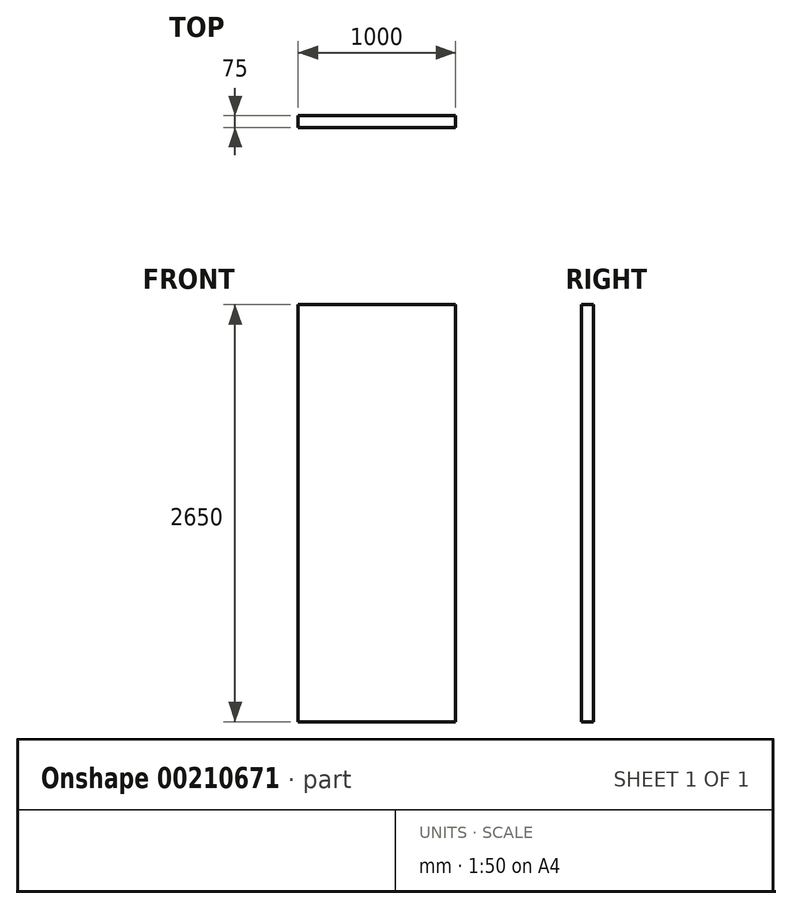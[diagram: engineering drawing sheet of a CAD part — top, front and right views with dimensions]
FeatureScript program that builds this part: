
annotation { "Feature Type Name" : "Feature", "Feature Type Description" : "" }
export const myFeature = defineFeature(function(context is Context, id is Id, definition is map)
    precondition{}
    {
        {
            var Q0;
            Q0=qCreatedBy(makeId("Front.planeOp"),FACE);
            var sketch = newSketch(context, id + "F0", { "sketchPlane" : qUnion([Q0])});
            skLineSegment(sketch, "E0.bottom", {"start": v(0, 0) * mm, "end": v(1000, 0) * mm});
            skLineSegment(sketch, "E0.top", {"start": v(0, 2650) * mm, "end": v(1000, 2650) * mm});
            skLineSegment(sketch, "E0.left", {"start": v(0, 0) * mm, "end": v(0, 2650) * mm});
            skLineSegment(sketch, "E0.right", {"start": v(1000, 0) * mm, "end": v(1000, 2650) * mm});
            skSolve(sketch);
        }
        {
            var Q0;
            Q0=makeQuery(id+"F0.imprint","IMPRINT",FACE,{"disambiguationData":[TD([[makeQuery(id+"F0.imprint","IMPRINT",EDGE,{"derivedFrom":sQuery(id+"F0.wireOp",EDGE,"E0.bottom")}),1.0]])]});
            extrude(context, id + "F1", {"entities" : qUnion([Q0]), "depth" : 75 * mm});
        }
    });
